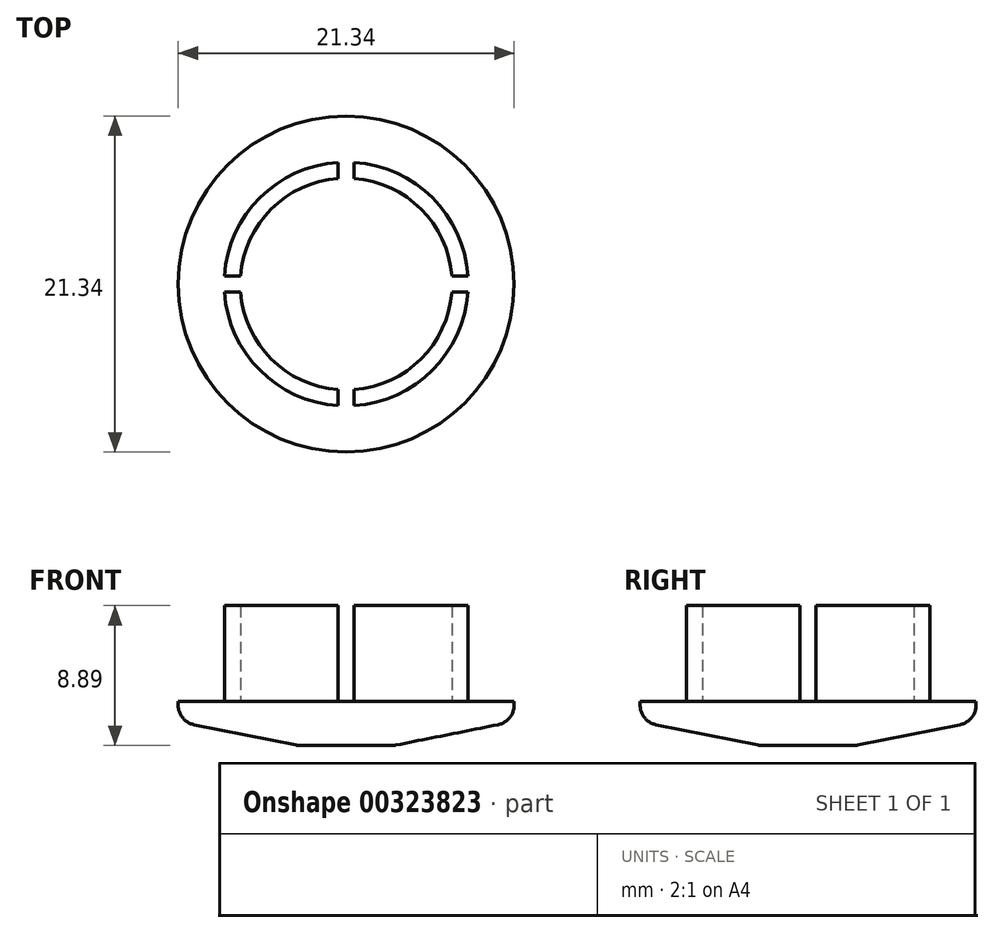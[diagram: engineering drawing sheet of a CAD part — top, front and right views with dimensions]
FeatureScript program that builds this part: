
annotation { "Feature Type Name" : "Feature", "Feature Type Description" : "" }
export const myFeature = defineFeature(function(context is Context, id is Id, definition is map)
    precondition{}
    {
        {
            var Q0;
            Q0=qCreatedBy(makeId("Top.planeOp"),FACE);
            var sketch = newSketch(context, id + "F0", { "sketchPlane" : qUnion([Q0])});
            skArc(sketch, "E0", {"start": v(-7.73, -0.5) * mm, "mid": v(-5.48, -5.48) * mm, "end": v(-0.5, -7.73) * mm});
            skArc(sketch, "E1", {"start": v(-6.71, -0.5) * mm, "mid": v(-4.76, -4.76) * mm, "end": v(-0.5, -6.71) * mm});
            skLineSegment(sketch, "E2.trimOffspring", {"start": v(-6.71, -0.5) * mm, "end": v(-7.73, -0.5) * mm});
            skLineSegment(sketch, "E3.trimOffspring", {"start": v(-7.73, 0.5) * mm, "end": v(-6.71, 0.5) * mm});
            skArc(sketch, "E4.trimOffspring", {"start": v(7.73, 0.5) * mm, "mid": v(5.48, 5.48) * mm, "end": v(0.5, 7.73) * mm});
            skArc(sketch, "E5.trimOffspring", {"start": v(6.71, 0.5) * mm, "mid": v(4.76, 4.76) * mm, "end": v(0.5, 6.71) * mm});
            skLineSegment(sketch, "E6.1.3.0", {"start": v(7.73, -0.5) * mm, "end": v(6.71, -0.5) * mm});
            skLineSegment(sketch, "E6.3.3.0", {"start": v(6.71, 0.5) * mm, "end": v(7.73, 0.5) * mm});
            skLineSegment(sketch, "E7.1.0", {"start": v(0.5, 7.73) * mm, "end": v(0.5, 6.71) * mm});
            skLineSegment(sketch, "E7.1.1", {"start": v(-0.5, 6.71) * mm, "end": v(-0.5, 7.73) * mm});
            skLineSegment(sketch, "E7.3.0", {"start": v(-0.5, -7.73) * mm, "end": v(-0.5, -6.71) * mm});
            skLineSegment(sketch, "E7.3.1", {"start": v(0.5, -6.71) * mm, "end": v(0.5, -7.73) * mm});
            skLineSegment(sketch, "E7.anchor1", {"start": v(0, 0) * mm, "end": v(-7.73, -0.5) * mm, "construction": true});
            skLineSegment(sketch, "E7.anchor2", {"start": v(0, 0) * mm, "end": v(0.5, -7.73) * mm, "construction": true});
            skArc(sketch, "E8.trimOffspring", {"start": v(0.44, -6.72) * mm, "mid": v(4.74, -4.78) * mm, "end": v(6.71, -0.5) * mm});
            skArc(sketch, "E9.trimOffspring", {"start": v(0.5, -7.73) * mm, "mid": v(5.48, -5.48) * mm, "end": v(7.73, -0.5) * mm});
            skArc(sketch, "E10.trimOffspring", {"start": v(-0.5, 7.73) * mm, "mid": v(-5.48, 5.48) * mm, "end": v(-7.73, 0.5) * mm});
            skArc(sketch, "E11.trimOffspring", {"start": v(-0.5, 6.71) * mm, "mid": v(-4.76, 4.76) * mm, "end": v(-6.71, 0.5) * mm});
            skSolve(sketch);
        }
        {
            var Q0;
            Q0=makeQuery(id+"F0.imprint","IMPRINT",FACE,{"disambiguationData":[TD([[makeQuery(id+"F0.imprint","IMPRINT",EDGE,{"derivedFrom":sQuery(id+"F0.wireOp",EDGE,"E4.trimOffspring")}),1.0]])]});
            var Q1;
            Q1=makeQuery(id+"F0.imprint","IMPRINT",FACE,{"disambiguationData":[TD([[makeQuery(id+"F0.imprint","IMPRINT",EDGE,{"derivedFrom":sQuery(id+"F0.wireOp",EDGE,"E3.trimOffspring")}),1.0]])]});
            var Q2;
            Q2=makeQuery(id+"F0.imprint","IMPRINT",FACE,{"disambiguationData":[TD([[makeQuery(id+"F0.imprint","IMPRINT",EDGE,{"derivedFrom":sQuery(id+"F0.wireOp",EDGE,"E0")}),1.0]])]});
            var Q3;
            {var subQ0=sQuery(id+"F0.wireOp",EDGE,"E6.1.3.0");Q3=makeQuery(id+"F0.imprint","IMPRINT",FACE,{"disambiguationData":[TD([[makeQuery(id+"F0.imprint","IMPRINT",EDGE,{"derivedFrom":subQ0}),1.0]])]});}
            extrude(context, id + "F1", {"entities" : qUnion([Q0, Q1, Q2, Q3]), "depth" : 6.35 * mm});
        }
        {
            var Q0;
            Q0=qCreatedBy(makeId("Top.planeOp"),FACE);
            var sketch = newSketch(context, id + "F2", { "sketchPlane" : qUnion([Q0])});
            skCircle(sketch, "E12", {"center": v(0, 0) * mm, "radius": 10.67 * mm});
            skSolve(sketch);
        }
        {
            var Q0;
            Q0=qSketchRegion(id+"F2",true);
            extrude(context, id + "F3", {"entities" : qUnion([Q0]), "oppositeDirection" : true, "depth" : 2.54 * mm});
        }
        {
            var Q0;
            Q0=makeQuery(id+"F3.opExtrude","CAP_FACE",FACE,{"disambiguationData":[OSD([sQuery(id+"F2.wireOp",EDGE,"E12")])],"isStart":true});
            extrude(context, id + "F4", {"entities" : qUnion([Q0]), "depth" : 0.25 * mm});
        }
        {
            var Q0;
            Q0=makeQuery(id+"F1.opExtrude","SWEPT_BODY",BODY,{"disambiguationData":[OSD([sQuery(id+"F0.wireOp",EDGE,"E0"),sQuery(id+"F0.wireOp",EDGE,"E1"),sQuery(id+"F0.wireOp",EDGE,"E2.trimOffspring"),sQuery(id+"F0.wireOp",EDGE,"E7.3.0")])]});
            var Q1;
            Q1=makeQuery(id+"F1.opExtrude","SWEPT_BODY",BODY,{"disambiguationData":[OSD([sQuery(id+"F0.wireOp",EDGE,"E3.trimOffspring"),sQuery(id+"F0.wireOp",EDGE,"E7.1.1"),sQuery(id+"F0.wireOp",EDGE,"E10.trimOffspring"),sQuery(id+"F0.wireOp",EDGE,"E11.trimOffspring")])]});
            var Q2;
            Q2=makeQuery(id+"F1.opExtrude","SWEPT_BODY",BODY,{"disambiguationData":[OSD([sQuery(id+"F0.wireOp",EDGE,"E4.trimOffspring"),sQuery(id+"F0.wireOp",EDGE,"E5.trimOffspring"),sQuery(id+"F0.wireOp",EDGE,"E7.1.0"),sQuery(id+"F0.wireOp",EDGE,"E6.3.3.0")])]});
            var Q3;
            Q3=makeQuery(id+"F1.opExtrude","SWEPT_BODY",BODY,{"disambiguationData":[OSD([sQuery(id+"F0.wireOp",EDGE,"E6.1.3.0"),sQuery(id+"F0.wireOp",EDGE,"E7.3.1"),sQuery(id+"F0.wireOp",EDGE,"E8.trimOffspring"),sQuery(id+"F0.wireOp",EDGE,"E9.trimOffspring")])]});
            var Q4;
            Q4=makeQuery(id+"F3.opExtrude","SWEPT_BODY",BODY,{"disambiguationData":[OSD([sQuery(id+"F2.wireOp",EDGE,"E12")])]});
            var Q5;
            Q5=makeQuery(id+"F4.opExtrude","SWEPT_BODY",BODY,{"disambiguationData":[OSD([sQuery(id+"F2.wireOp",EDGE,"E12")])]});
            booleanBodies(context, id + "F5", {"operationType" : BooleanOperationType.UNION, "tools" : qUnion([Q0, Q1, Q2, Q3, Q4, Q5])});
        }
        {
            var Q0;
            Q0=makeQuery(id+"F3.opExtrude","CAP_EDGE",EDGE,{"disambiguationData":[OSD([sQuery(id+"F2.wireOp",EDGE,"E12")])],"isStart":false});
            chamfer(context, id + "F6", {"entities" : qUnion([Q0]), "chamferType" : ChamferType.TWO_OFFSETS, "width1" : 1.52 * mm, "oppositeDirection" : false, "width2" : 7.62 * mm, "tangentPropagation" : true});
        }
        {
            var Q0;
            {var subQ0=sQuery(id+"F2.wireOp",EDGE,"E12");Q0=makeQuery(id+"F6.opChamfer","BLEND_EDGE",EDGE,{"blendedFrom":[makeQuery(id+"F3.opExtrude","CAP_EDGE",EDGE,{"disambiguationData":[OSD([subQ0])],"isStart":false}),makeQuery(id+"F5.opBoolean","MERGE",FACE,{"derivedFrom":[makeQuery(id+"F3.opExtrude","SWEPT_FACE",FACE,{"disambiguationData":[OSD([subQ0])]}),makeQuery(id+"F4.opExtrude","SWEPT_FACE",FACE,{"disambiguationData":[OSD([subQ0])]})]})],"blendedInto":[makeQuery(id+"F5.opBoolean","MERGE",FACE,{"derivedFrom":[makeQuery(id+"F3.opExtrude","SWEPT_FACE",FACE,{"disambiguationData":[OSD([subQ0])]}),makeQuery(id+"F4.opExtrude","SWEPT_FACE",FACE,{"disambiguationData":[OSD([subQ0])]})]})]});}
            var Q1;
            Q1=makeQuery(id+"F3.opExtrude","CAP_FACE",FACE,{"disambiguationData":[OSD([sQuery(id+"F2.wireOp",EDGE,"E12")])],"isStart":false});
            fillet(context, id + "F7", {"entities" : qUnion([Q0, Q1]), "radius" : 1.27 * mm, "tangentPropagation" : true, "allowEdgeOverflow" : false});
        }
    });
